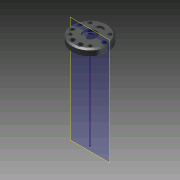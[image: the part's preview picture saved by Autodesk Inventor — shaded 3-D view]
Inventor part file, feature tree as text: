
AUTODESK INVENTOR PART (.ipt)
format: ipt  version: 2014 (Build 180170000, 170)  size: 2,363,392 bytes
history: native  units: mm
features: other x2, sketch x2, extrude x1, imported_body x1
ambient origin geometry x8: Origin, YZ Plane, XZ Plane, XY Plane, X Axis, Y Axis, Z Axis, Center Point
bodies: Body1 (feature_tree)
feature tree (6):
  other  "vis_standard"
  other  "BALL SCREW STROKE STD.ipt1"
  extrude  "Extrusión1"  Depth=35.5mm
  sketch  "Boceto 3D1"  dims[d0=261.2mm d1=35.5mm]
  imported_body  "Base1"
  sketch  "Boceto1"  dims[d2=20.0mm d3=25.0mm d4=0.0mm d5=0.0mm]
